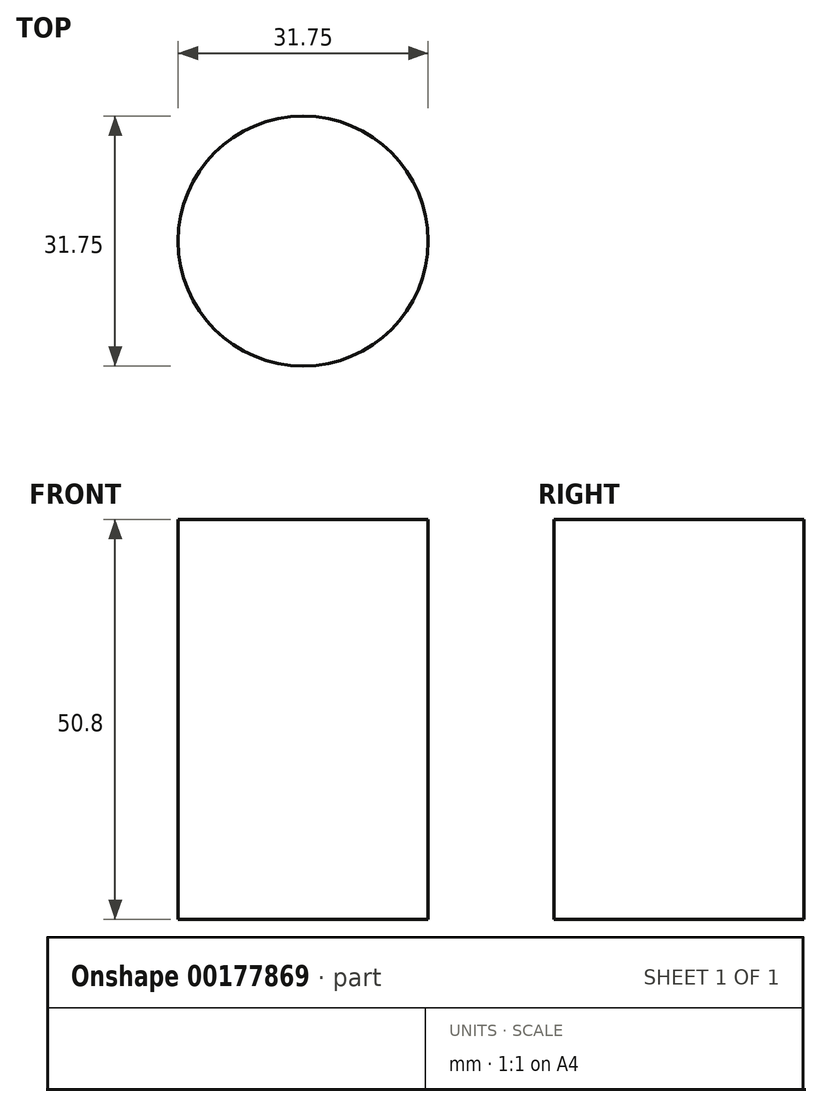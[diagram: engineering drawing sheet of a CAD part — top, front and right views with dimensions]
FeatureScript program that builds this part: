
annotation { "Feature Type Name" : "Feature", "Feature Type Description" : "" }
export const myFeature = defineFeature(function(context is Context, id is Id, definition is map)
    precondition{}
    {
        {
            var Q0;
            Q0=qCreatedBy(makeId("Top.planeOp"),FACE);
            var sketch = newSketch(context, id + "F0", { "sketchPlane" : qUnion([Q0])});
            skCircle(sketch, "E0", {"center": v(-21.14, 17.52) * mm, "radius": 15.88 * mm});
            skSolve(sketch);
        }
        {
            var Q0;
            Q0 = qSketchRegion(id + "F0", true);
            extrude(context, id + "F1", {"entities" : qUnion([Q0]), "depth" : 50.8 * mm});
        }
    });
